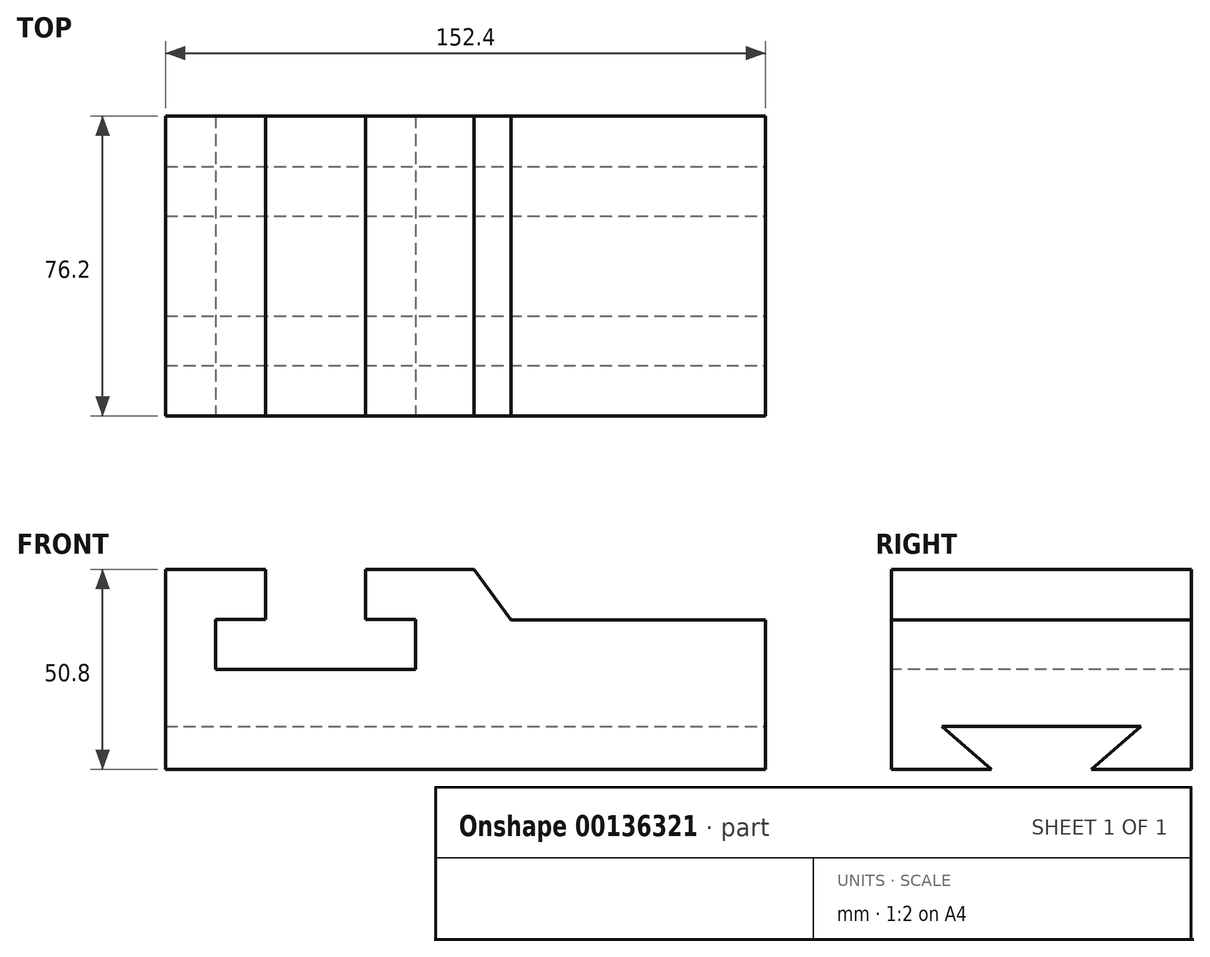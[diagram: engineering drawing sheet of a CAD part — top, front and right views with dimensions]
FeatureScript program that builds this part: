
annotation { "Feature Type Name" : "Feature", "Feature Type Description" : "" }
export const myFeature = defineFeature(function(context is Context, id is Id, definition is map)
    precondition{}
    {
        {
            var Q0;
            Q0=qCreatedBy(makeId("Top.planeOp"),FACE);
            var sketch = newSketch(context, id + "F0", { "sketchPlane" : qUnion([Q0])});
            skLineSegment(sketch, "E0", {"start": v(-78.37, 0) * mm, "end": v(-78.37, -38.1) * mm});
            skLineSegment(sketch, "E1", {"start": v(-78.37, -38.1) * mm, "end": v(74.03, -38.1) * mm});
            skLineSegment(sketch, "E2", {"start": v(74.03, -38.1) * mm, "end": v(74.03, 0) * mm});
            skLineSegment(sketch, "E3", {"start": v(74.03, 0) * mm, "end": v(-78.37, 0) * mm});
            skSolve(sketch);
        }
        {
            var Q0;
            Q0=makeQuery(id+"F0.imprint","IMPRINT",FACE,{"disambiguationData":[TD([[makeQuery(id+"F0.imprint","IMPRINT",EDGE,{"derivedFrom":sQuery(id+"F0.wireOp",EDGE,"E0")}),1.0]])]});
            extrude(context, id + "F1", {"entities" : qUnion([Q0]), "depth" : 50.8 * mm});
        }
        {
            var Q0;
            Q0=makeQuery(id+"F1.opExtrude","SWEPT_FACE",FACE,{"disambiguationData":[OSD([sQuery(id+"F0.wireOp",EDGE,"E2")])]});
            var sketch = newSketch(context, id + "F2", { "sketchPlane" : qUnion([Q0])});
            skLineSegment(sketch, "E4", {"start": v(0, 0) * mm, "end": v(-12.7, 0) * mm});
            skLineSegment(sketch, "E5", {"start": v(-25.33, 10.88) * mm, "end": v(-12.7, 0) * mm});
            skLineSegment(sketch, "E6", {"start": v(-25.33, 10.88) * mm, "end": v(0, 10.88) * mm});
            skLineSegment(sketch, "E7", {"start": v(0, 10.88) * mm, "end": v(0, 0) * mm});
            skLineSegment(sketch, "E8", {"start": v(-12.7, 0) * mm, "end": v(0, 0) * mm});
            skSolve(sketch);
        }
        {
            var Q0;
            Q0=makeQuery(id+"F2.imprint","IMPRINT",FACE,{"disambiguationData":[TD([[makeQuery(id+"F2.imprint","IMPRINT",EDGE,{"derivedFrom":sQuery(id+"F2.wireOp",EDGE,"E5")}),1.0]])]});
            extrude(context, id + "F3", {"entities" : qUnion([Q0]), "operationType" : NewBodyOperationType.REMOVE, "endBound" : BoundingType.THROUGH_ALL, "oppositeDirection" : true, "depth" : 25.4 * mm});
        }
        {
            var Q0;
            Q0=makeQuery(id+"F1.opExtrude","SWEPT_FACE",FACE,{"disambiguationData":[OSD([sQuery(id+"F0.wireOp",EDGE,"E1")])]});
            var sketch = newSketch(context, id + "F4", { "sketchPlane" : qUnion([Q0])});
            skLineSegment(sketch, "E9", {"start": v(-78.37, 50.8) * mm, "end": v(-52.97, 50.8) * mm});
            skLineSegment(sketch, "E10", {"start": v(-52.97, 50.8) * mm, "end": v(-52.97, 38.1) * mm});
            skLineSegment(sketch, "E11", {"start": v(-52.97, 38.1) * mm, "end": v(-65.67, 38.1) * mm});
            skLineSegment(sketch, "E12", {"start": v(-65.67, 38.1) * mm, "end": v(-65.67, 25.4) * mm});
            skPoint(sketch, "E12.endSnap0", {"position": v(-78.37, 25.4) * mm});
            skLineSegment(sketch, "E13", {"start": v(-65.67, 25.4) * mm, "end": v(-14.87, 25.4) * mm});
            skLineSegment(sketch, "E14", {"start": v(-14.87, 25.4) * mm, "end": v(-14.87, 38.1) * mm});
            skLineSegment(sketch, "E15", {"start": v(-14.87, 38.1) * mm, "end": v(-27.57, 38.1) * mm});
            skLineSegment(sketch, "E16", {"start": v(-27.57, 38.1) * mm, "end": v(-27.57, 50.8) * mm});
            skLineSegment(sketch, "E17", {"start": v(-52.97, 50.8) * mm, "end": v(-27.57, 50.8) * mm});
            skSolve(sketch);
        }
        {
            var Q0;
            Q0=makeQuery(id+"F4.imprint","IMPRINT",FACE,{"disambiguationData":[TD([[makeQuery(id+"F4.imprint","IMPRINT",EDGE,{"derivedFrom":sQuery(id+"F4.wireOp",EDGE,"E10")}),1.0]])]});
            extrude(context, id + "F5", {"entities" : qUnion([Q0]), "operationType" : NewBodyOperationType.REMOVE, "endBound" : BoundingType.THROUGH_ALL, "oppositeDirection" : true, "depth" : 25.4 * mm});
        }
        {
            var Q0;
            Q0=makeQuery(id+"F4.imprint","IMPRINT",FACE,{"disambiguationData":[TD([[makeQuery(id+"F4.imprint","IMPRINT",EDGE,{"derivedFrom":sQuery(id+"F4.wireOp",EDGE,"E9")}),-1.0]])]});
            var sketch = newSketch(context, id + "F6", { "sketchPlane" : qUnion([Q0])});
            skLineSegment(sketch, "E18", {"start": v(0, 50.8) * mm, "end": v(0, 50.8) * mm});
            skLineSegment(sketch, "E19", {"start": v(0, 50.8) * mm, "end": v(9.34, 38) * mm});
            skLineSegment(sketch, "E20", {"start": v(9.34, 38) * mm, "end": v(74.6, 38) * mm});
            skLineSegment(sketch, "E21", {"start": v(74.6, 38) * mm, "end": v(74.6, 50.8) * mm});
            skLineSegment(sketch, "E22", {"start": v(74.6, 50.8) * mm, "end": v(0, 50.8) * mm});
            skSolve(sketch);
        }
        {
            var Q0;
            Q0=qSketchRegion(id+"F6",true);
            extrude(context, id + "F7", {"entities" : qUnion([Q0]), "operationType" : NewBodyOperationType.REMOVE, "endBound" : BoundingType.THROUGH_ALL, "oppositeDirection" : true, "depth" : 25.4 * mm});
        }
        {
            var Q0;
            Q0=makeQuery(id+"F1.opExtrude","SWEPT_BODY",BODY,{"disambiguationData":[OSD([sQuery(id+"F0.wireOp",EDGE,"E0"),sQuery(id+"F0.wireOp",EDGE,"E1"),sQuery(id+"F0.wireOp",EDGE,"E2"),sQuery(id+"F0.wireOp",EDGE,"E3")])]});
            var Q1;
            Q1=qCreatedBy(makeId("Front.planeOp"),FACE);
            mirror(context, id + "F8", {"operationType" : NewBodyOperationType.ADD, "entities" : qUnion([Q0]), "mirrorPlane" : qUnion([Q1])});
        }
    });
